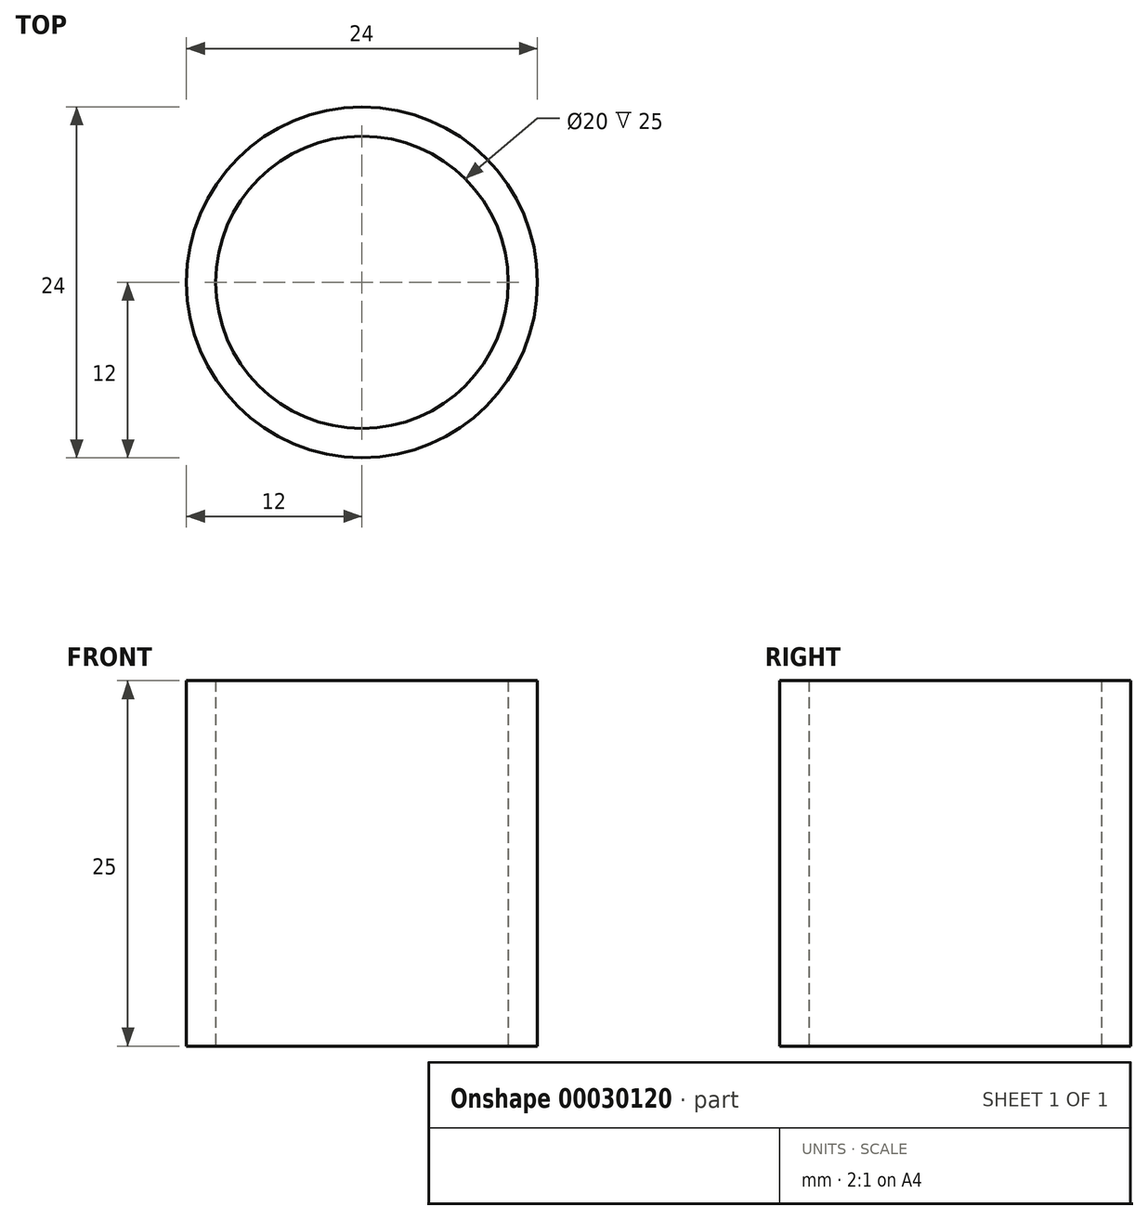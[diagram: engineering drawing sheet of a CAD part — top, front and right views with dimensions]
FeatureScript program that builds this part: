
annotation { "Feature Type Name" : "Feature", "Feature Type Description" : "" }
export const myFeature = defineFeature(function(context is Context, id is Id, definition is map)
    precondition{}
    {
        {
            var Q0;
            Q0=qCreatedBy(makeId("Top.planeOp"),FACE);
            var sketch = newSketch(context, id + "F0", { "sketchPlane" : qUnion([Q0])});
            skCircle(sketch, "E0", {"center": v(0, 0) * mm, "radius": 10 * mm});
            skCircle(sketch, "E1.0", {"center": v(0, 0) * mm, "radius": 12 * mm});
            skSolve(sketch);
        }
        {
            var Q0;
            Q0=makeQuery(id+"F0.imprint","IMPRINT",FACE,{"disambiguationData":[TD([[makeQuery(id+"F0.imprint","IMPRINT",EDGE,{"derivedFrom":sQuery(id+"F0.wireOp",EDGE,"E0")}),-1.0]])]});
            extrude(context, id + "F1", {"entities" : qUnion([Q0]), "depth" : 25 * mm});
        }
    });
